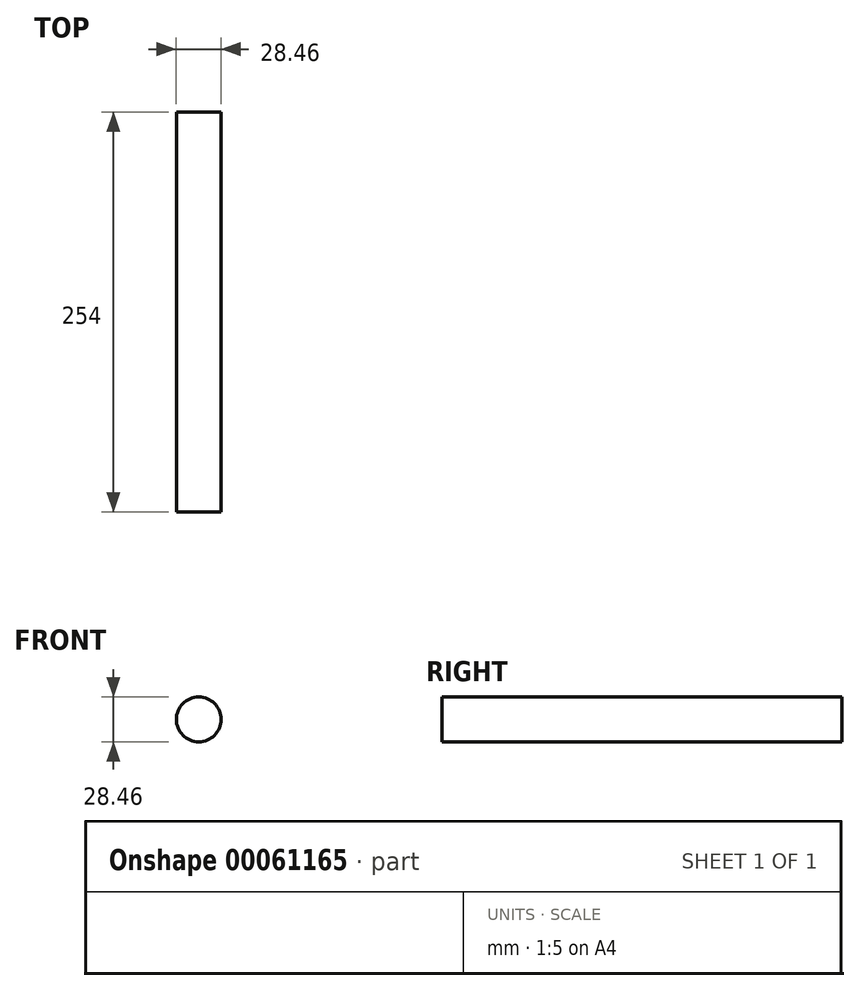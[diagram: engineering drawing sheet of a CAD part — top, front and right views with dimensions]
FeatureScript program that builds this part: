
annotation { "Feature Type Name" : "Feature", "Feature Type Description" : "" }
export const myFeature = defineFeature(function(context is Context, id is Id, definition is map)
    precondition{}
    {
        {
            var Q0;
            Q0=qCreatedBy(makeId("Front.planeOp"),FACE);
            var sketch = newSketch(context, id + "F0", { "sketchPlane" : qUnion([Q0])});
            skCircle(sketch, "E0", {"center": v(0, 0) * mm, "radius": 22.23 * mm});
            skArc(sketch, "E1", {"start": v(-9.73, 10.38) * mm, "mid": v(6.38, -12.71) * mm, "end": v(-2.5, 14) * mm});
            skArc(sketch, "E2", {"start": v(-2.5, 14) * mm, "mid": v(-5.23, 13.23) * mm, "end": v(-7.75, 11.93) * mm});
            skArc(sketch, "E3", {"start": v(-7.75, 11.93) * mm, "mid": v(-8.77, 11.2) * mm, "end": v(-9.73, 10.38) * mm});
            skSolve(sketch);
        }
        {
            var Q0;
            Q0=makeQuery(id+"F0.imprint","IMPRINT",FACE,{"disambiguationData":[TD([[makeQuery(id+"F0.imprint","IMPRINT",EDGE,{"derivedFrom":sQuery(id+"F0.wireOp",EDGE,"E1")}),1.0]])]});
            extrude(context, id + "F1", {"entities" : qUnion([Q0]), "depth" : 254 * mm});
        }
    });
